# Revit family: Festpunkthalterung HV3_
name_source: partatom
category: Allgemeines Modell
revit_build: Autodesk Revit 2018 (Build: 20190510_1515(x64)
units: mm (PartAtom-declared; Revit-internal decimal feet)

## family parameters
Basisbauteil = Fläche
Beim Laden mit Abzugskörper schneiden = Nein
Bemaßung runder Anschluss = Durchmesser verwenden
Gemeinsam genutzt = Ja
Kann Basisbauteil für Bewehrung sein = Nein
Raumberechnungspunkt = Nein
Teiletyp = Normal

## types (21) — shared parameters
Anzahl Rohrschellen = 3
Anzugsmoment Hammersperrkopf = 120 Nm
Artikelnummer = 00200407/fvz
Breite Material Rohrschelle = 50 mm
EAN = 4250928400024
Fabrikat = MEFA
Gewicht = 5.68 kg
Gewicht pro Bauteil = 5.68 kg
Kurztext1 = Festpunkthalterung HV 3
Kurztext2 = 64 - 406 mm Fx 30 kN 164 - 216 mm
Länge = 160 mm  [stored 0.524934 ft]
Material = Stahl
Mengeneinheit = St
Rohrschellentyp = Titan HD
Stärke Material Rohrschelle = 5 mm
Vorgabe-Ansicht = 1219 mm
max. Achshöhe = 216 mm
max. Rohraußendurchmesser = 406 mm  [stored 1.33202 ft]
max. zul. Last Fx = 6.74 kip
max. zul. Last Fz = 4.05 kip
max. zul. Last Fz mit 3 Schellen = 40 kN
min. Achshöhe = 164 mm
min. Rohraußendurchmesser = 64 mm  [stored 0.209974 ft]
vpe = 1

## per-type parameters (varying)
| type | S |
| HV3 Ø64 mm | 112 mm  [stored 0.367454 ft] |
| HV3 Ø76mm | 124 mm  [stored 0.406824 ft] |
| HV3 Ø89mm | 138 mm  [stored 0.452756 ft] |
| HV3 Ø108mm | 157 mm  [stored 0.515092 ft] |
| HV3 Ø110mm | 159 mm  [stored 0.521654 ft] |
| HV3 Ø114mm | 163 mm  [stored 0.534777 ft] |
| HV3 Ø133mm | 183 mm |
| HV3 Ø135mm | 185 mm  [stored 0.606955 ft] |
| HV3 Ø140mm | 190 mm |
| HV3 Ø160mm | 210 mm  [stored 0.688976 ft] |
| HV3 Ø165mm | 215 mm |
| HV3 Ø168mm | 218 mm  [stored 0.715223 ft] |
| HV3 Ø194mm | 244 mm  [stored 0.800525 ft] |
| HV3 Ø200mm | 250 mm  [stored 0.82021 ft] |
| HV3 Ø210mm | 261 mm |
| HV3 Ø219mm | 270 mm  [stored 0.885827 ft] |
| HV3 Ø267mm | 318 mm  [stored 1.04331 ft] |
| HV3 Ø273mm | 324 mm  [stored 1.06299 ft] |
| HV3 Ø324mm | 375 mm  [stored 1.23031 ft] |
| HV3 Ø356mm | 407 mm  [stored 1.3353 ft] |
| HV3 Ø368mm | 419 mm |

note: [stored X ft] marks values corroborated as IEEE doubles in the binary element streams (Revit-internal decimal feet)

## geometry (parser evidence)
native form markers: Sweep x5
no freeform markers — native parametric forms only
